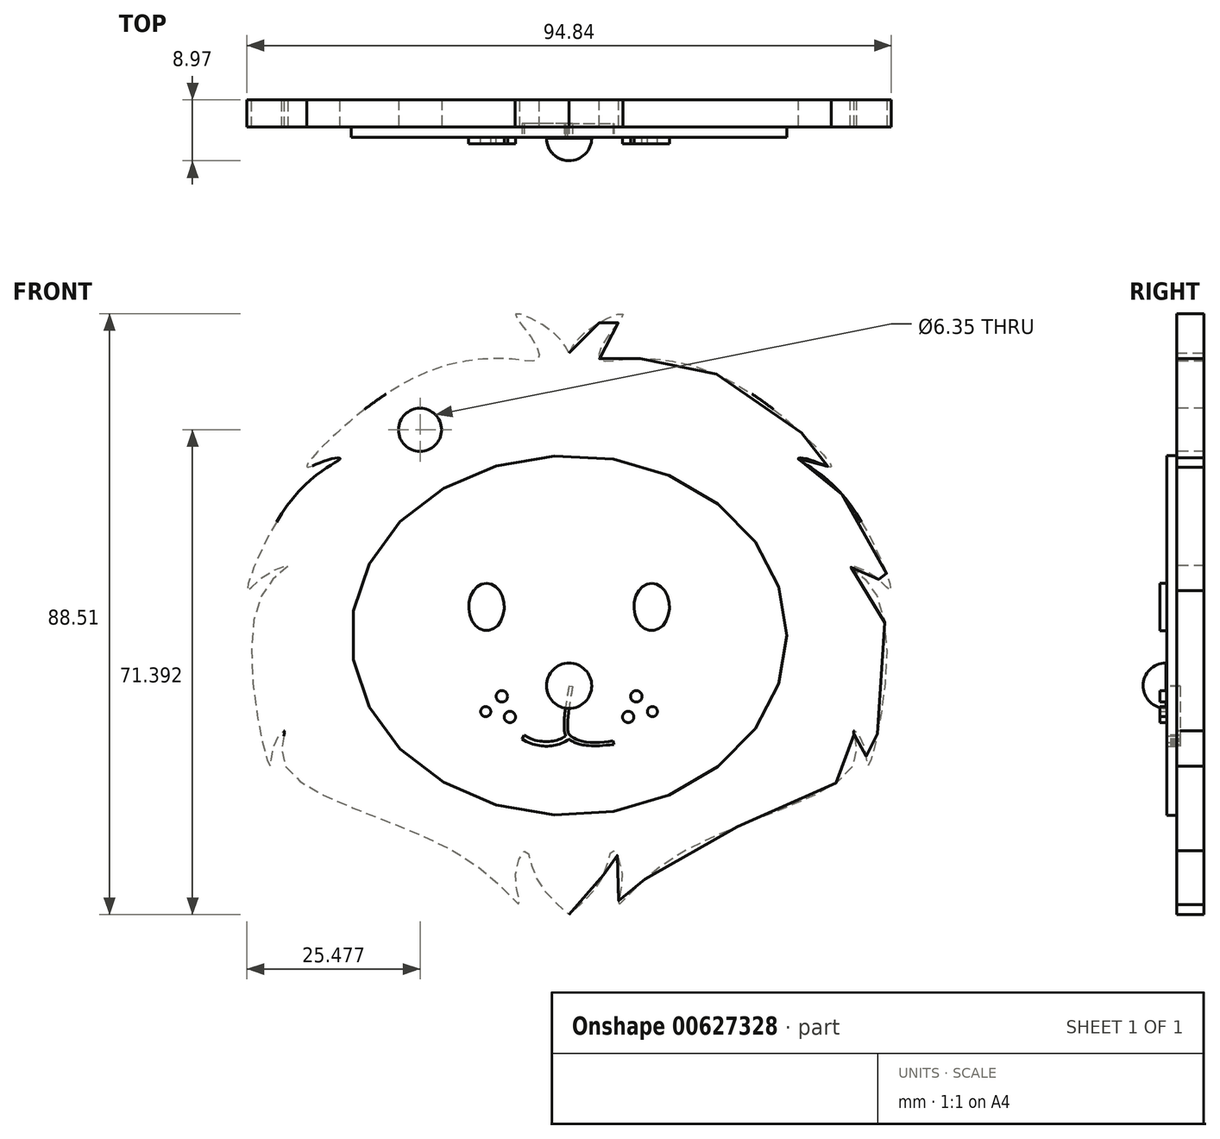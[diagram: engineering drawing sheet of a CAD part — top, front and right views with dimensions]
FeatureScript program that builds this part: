
annotation { "Feature Type Name" : "Feature", "Feature Type Description" : "" }
export const myFeature = defineFeature(function(context is Context, id is Id, definition is map)
    precondition{}
    {
        {
            var Q0;
            Q0=qCreatedBy(makeId("Front.planeOp"),FACE);
            var sketch = newSketch(context, id + "F0", { "sketchPlane" : qUnion([Q0])});
            skFitSpline(sketch, "E0", {"points": [v(0, 48.97) * mm, v(2.72, 52.32) * mm, v(7.89, 54.75) * mm, v(5.45, 51.1) * mm, v(4.54, 48.06) * mm, v(8.19, 48.06) * mm, v(24.6, 44.42) * mm, v(38.58, 32.26) * mm, v(35.85, 33.17) * mm, v(33.72, 33.47) * mm, v(40.1, 28.3) * mm, v(47.4, 14.02) * mm, v(44.97, 16.15) * mm, v(41.32, 17.67) * mm, v(45.88, 11.9) * mm, v(44.05, -11.81) * mm, v(43.45, -8.77) * mm, v(41.93, -6.65) * mm, v(41.93, -11.5) * mm, v(15.48, -25.19) * mm, v(7.28, -32.18) * mm, v(7.89, -27.92) * mm, v(6.37, -24.28) * mm, v(5.15, -27.62) * mm, v(0, -33.7) * mm], "startDerivative": vector(53.9, 99.14) * mm, "endDerivative": vector(-141.36, -126.3) * mm});
            skLineSegment(sketch, "E1", {"start": v(0, 48.97) * mm, "end": v(0, -33.46) * mm});
            skFitSpline(sketch, "E2.MirrorCS", {"points": [v(0, 48.97) * mm, v(-2.72, 52.32) * mm, v(-7.89, 54.75) * mm, v(-5.45, 51.1) * mm, v(-4.54, 48.06) * mm, v(-8.19, 48.06) * mm, v(-24.6, 44.42) * mm, v(-38.58, 32.26) * mm, v(-35.85, 33.17) * mm, v(-33.72, 33.47) * mm, v(-40.1, 28.3) * mm, v(-47.4, 14.02) * mm, v(-44.97, 16.15) * mm, v(-41.32, 17.67) * mm, v(-45.88, 11.9) * mm, v(-44.05, -11.81) * mm, v(-43.45, -8.77) * mm, v(-41.93, -6.65) * mm, v(-41.93, -11.5) * mm, v(-15.48, -25.19) * mm, v(-7.28, -32.18) * mm, v(-7.89, -27.92) * mm, v(-6.37, -24.28) * mm, v(-5.15, -27.62) * mm, v(0, -33.7) * mm], "startDerivative": vector(-53.9, 99.14) * mm, "endDerivative": vector(141.36, -126.3) * mm});
            skFitSpline(sketch, "E3.MirrorCS", {"points": [v(0, 48.97) * mm, v(-2.72, 52.32) * mm, v(-7.89, 54.75) * mm, v(-5.45, 51.1) * mm, v(-4.54, 48.06) * mm, v(-8.19, 48.06) * mm, v(-24.6, 44.42) * mm, v(-38.58, 32.26) * mm, v(-35.85, 33.17) * mm, v(-33.72, 33.47) * mm, v(-40.1, 28.3) * mm, v(-47.4, 14.02) * mm, v(-44.97, 16.15) * mm, v(-41.32, 17.67) * mm, v(-45.88, 11.9) * mm, v(-44.05, -11.81) * mm, v(-43.45, -8.77) * mm, v(-41.93, -6.65) * mm, v(-41.93, -11.5) * mm, v(-15.48, -25.19) * mm, v(-7.28, -32.18) * mm, v(-7.89, -27.92) * mm, v(-6.37, -24.28) * mm, v(-5.15, -27.62) * mm, v(0, -33.7) * mm], "startDerivative": vector(-53.9, 99.14) * mm, "endDerivative": vector(141.36, -126.3) * mm});
            skSolve(sketch);
        }
        {
            var Q0;
            Q0=makeQuery(id+"F0.imprint","IMPRINT",FACE,{"disambiguationData":[TD([[makeQuery(id+"F0.imprint","IMPRINT",EDGE,{"derivedFrom":sQuery(id+"F0.wireOp",EDGE,"E0")}),-1.0]])]});
            var Q1;
            Q1 = qSketchRegion(id + "F0", true);
            extrude(context, id + "F1", {"entities" : qUnion([Q0, Q1]), "depth" : 4 * mm, "offsetDistance" : 25.4 * mm});
        }
        {
            var Q0;
            Q0=makeQuery(id+"F1.opExtrude","CAP_FACE",FACE,{"disambiguationData":[OSD([sQuery(id+"F0.wireOp",EDGE,"E0"),sQuery(id+"F0.wireOp",EDGE,"E3.MirrorCS")])],"isStart":false});
            var sketch = newSketch(context, id + "F2", { "sketchPlane" : qUnion([Q0])});
            skEllipse(sketch, "E4", {"center": v(0, 7.43) * mm, "majorRadius": 32.07 * mm, "minorRadius": 26.48 * mm, "majorAxis": v(1, 0)});
            skSolve(sketch);
        }
        {
            var Q0;
            Q0 = qSketchRegion(id + "F2", true);
            extrude(context, id + "F3", {"entities" : qUnion([Q0]), "operationType" : NewBodyOperationType.ADD, "depth" : 1.5 * mm, "offsetDistance" : 25.4 * mm});
        }
        {
            var Q0;
            Q0=qCreatedBy(makeId("Top.planeOp"),FACE);
            var sketch = newSketch(context, id + "F4", { "sketchPlane" : qUnion([Q0])});
            skArc(sketch, "E5", {"start": v(0, -8.97) * mm, "mid": v(2.36, -8) * mm, "end": v(3.33, -5.63) * mm});
            skLineSegment(sketch, "E6", {"start": v(0, -8.97) * mm, "end": v(0, -5.63) * mm});
            skLineSegment(sketch, "E7", {"start": v(0, -5.63) * mm, "end": v(3.33, -5.63) * mm});
            skSolve(sketch);
        }
        {
            var Q0;
            Q0 = qSketchRegion(id + "F4", true);
            var Q1;
            Q1=sQuery(id+"F4.wireOp",EDGE,"E6");
            revolve(context, id + "F5", {"entities" : qUnion([Q0]), "axis" : qUnion([Q1]), "revolveType" : RevolveType.FULL});
        }
        {
            var Q0;
            Q0=makeQuery(id+"F3.opExtrude","CAP_FACE",FACE,{"disambiguationData":[OSD([sQuery(id+"F2.wireOp",EDGE,"E4")])],"isStart":false});
            var sketch = newSketch(context, id + "F6", { "sketchPlane" : qUnion([Q0])});
            skEllipse(sketch, "E8", {"center": v(-12.16, 11.61) * mm, "majorRadius": 3.5 * mm, "minorRadius": 2.61 * mm, "majorAxis": v(0, 1)});
            skEllipse(sketch, "E9.MirrorC", {"center": v(12.16, 11.61) * mm, "majorRadius": 3.5 * mm, "minorRadius": 2.61 * mm, "majorAxis": v(0, 1)});
            skSolve(sketch);
        }
        {
            var Q0;
            Q0 = qSketchRegion(id + "F6", true);
            extrude(context, id + "F7", {"entities" : qUnion([Q0]), "operationType" : NewBodyOperationType.ADD, "depth" : 1 * mm, "offsetDistance" : 25.4 * mm});
        }
        {
            var Q0;
            Q0=makeQuery(id+"F3.opExtrude","CAP_FACE",FACE,{"disambiguationData":[OSD([sQuery(id+"F2.wireOp",EDGE,"E4")])],"isStart":false});
            var sketch = newSketch(context, id + "F8", { "sketchPlane" : qUnion([Q0])});
            skCircle(sketch, "E10", {"center": v(9.9, -1.56) * mm, "radius": 0.84 * mm});
            skCircle(sketch, "E11", {"center": v(12.27, -3.8) * mm, "radius": 0.75 * mm});
            skCircle(sketch, "E12", {"center": v(8.71, -4.59) * mm, "radius": 0.83 * mm});
            skCircle(sketch, "E13.MirrorC", {"center": v(-9.9, -1.56) * mm, "radius": 0.84 * mm});
            skCircle(sketch, "E14.MirrorC", {"center": v(-12.27, -3.8) * mm, "radius": 0.75 * mm});
            skCircle(sketch, "E15.MirrorC", {"center": v(-8.71, -4.59) * mm, "radius": 0.83 * mm});
            skSolve(sketch);
        }
        {
            var Q0;
            Q0 = qSketchRegion(id + "F8", true);
            extrude(context, id + "F9", {"entities" : qUnion([Q0]), "operationType" : NewBodyOperationType.ADD, "depth" : 1 * mm, "offsetDistance" : 25.4 * mm});
        }
        {
            var Q0;
            Q0=makeQuery(id+"F1.opExtrude","CAP_FACE",FACE,{"disambiguationData":[OSD([sQuery(id+"F0.wireOp",EDGE,"E0"),sQuery(id+"F0.wireOp",EDGE,"E3.MirrorCS")])],"isStart":false});
            var sketch = newSketch(context, id + "F10", { "sketchPlane" : qUnion([Q0])});
            skCircle(sketch, "E16", {"center": v(-21.94, 37.7) * mm, "radius": 3.8 * mm});
            skSolve(sketch);
        }
        {
            var Q0;
            Q0=sQuery(id+"F10.wireOp",VERTEX,"E16.center");
            var Q1;
            Q1=makeQuery(id+"F1.opExtrude","SWEPT_BODY",BODY,{"disambiguationData":[OSD([sQuery(id+"F0.wireOp",EDGE,"E0"),sQuery(id+"F0.wireOp",EDGE,"E3.MirrorCS")])]});
            hole(context, id + "F11", {"style" : HoleStyle.SIMPLE, "endStyle" : HoleEndStyle.THROUGH, "holeDiameter" : 6.35 * mm, "majorDiameter" : 6.35 * mm, "isTappedThrough" : true, "tappedDepth" : 12.7 * mm, "tapClearance" : 3, "locations" : qUnion([Q0]), "scope" : qUnion([Q1])});
        }
        {
            var Q0;
            Q0=makeQuery(id+"F3.opExtrude","CAP_FACE",FACE,{"disambiguationData":[OSD([sQuery(id+"F2.wireOp",EDGE,"E4")])],"isStart":false});
            var sketch = newSketch(context, id + "F12", { "sketchPlane" : qUnion([Q0])});
            skFitSpline(sketch, "E17", {"points": [v(0, 0) * mm, v(-0.64, -6.92) * mm, v(0, -7.85) * mm, v(6.57, -8.63) * mm], "startDerivative": vector(-3.49, -17.73) * mm, "endDerivative": vector(32.8, 4.3) * mm});
            skFitSpline(sketch, "E18", {"points": [v(0, -7.85) * mm, v(-3.2, -8.88) * mm, v(-6.95, -7.85) * mm], "startDerivative": vector(-6.45, -4.56) * mm, "endDerivative": vector(-7.43, 4.46) * mm});
            skFitSpline(sketch, "E19.0", {"points": [v(-0.4, -7.3) * mm, v(-0.64, -7.46) * mm, v(-1.11, -7.74) * mm, v(-1.82, -8.01) * mm, v(-2.55, -8.17) * mm, v(-3.32, -8.21) * mm, v(-4.11, -8.16) * mm, v(-5.2, -7.95) * mm, v(-6.03, -7.6) * mm, v(-6.6, -7.26) * mm]});
            skFitSpline(sketch, "E20.0", {"points": [v(0.52, -0.1) * mm, v(0.38, -0.83) * mm, v(0.17, -2.02) * mm, v(-0.04, -3.58) * mm, v(-0.15, -4.68) * mm, v(-0.2, -5.66) * mm, v(-0.19, -6.32) * mm, v(-0.14, -6.71) * mm, v(-0.1, -6.93) * mm, v(-0.04, -7.06) * mm, v(0.01, -7.15) * mm, v(0.08, -7.23) * mm, v(0.17, -7.3) * mm, v(0.26, -7.38) * mm, v(0.36, -7.46) * mm, v(0.5, -7.56) * mm, v(0.7, -7.68) * mm, v(0.98, -7.83) * mm, v(1.43, -8.02) * mm, v(2.19, -8.2) * mm, v(3.6, -8.35) * mm, v(5.16, -8.28) * mm, v(6.5, -8.1) * mm]});
            skLineSegment(sketch, "E21", {"start": v(6.5, -8.1) * mm, "end": v(6.57, -8.63) * mm});
            skLineSegment(sketch, "E22", {"start": v(0, 0) * mm, "end": v(0.52, -0.1) * mm});
            skLineSegment(sketch, "E23", {"start": v(-6.6, -7.26) * mm, "end": v(-6.95, -7.85) * mm});
            skPoint(sketch, "E24", {"position": v(-0.5, -7.32) * mm});
            skLineSegment(sketch, "E25", {"start": v(-0.59, -7.42) * mm, "end": v(-0.5, -7.32) * mm});
            skSolve(sketch);
        }
        {
            var Q0;
            Q0 = qSketchRegion(id + "F12", true);
            extrude(context, id + "F13", {"entities" : qUnion([Q0]), "operationType" : NewBodyOperationType.REMOVE, "oppositeDirection" : true, "depth" : 1 * mm, "offsetDistance" : 25.4 * mm});
        }
        {
            var Q0;
            Q0=makeQuery(id+"F13.boolean.opBoolean","COPY",FACE,{"derivedFrom":makeQuery(id+"F13.opExtrude","CAP_FACE",FACE,{"disambiguationData":[OSD([sQuery(id+"F12.wireOp",EDGE,"E17"),sQuery(id+"F12.wireOp",EDGE,"E18"),sQuery(id+"F12.wireOp",EDGE,"E19.0"),sQuery(id+"F12.wireOp",EDGE,"E20.0"),sQuery(id+"F12.wireOp",EDGE,"E21"),sQuery(id+"F12.wireOp",EDGE,"E22"),sQuery(id+"F12.wireOp",EDGE,"E23"),sQuery(id+"F12.wireOp",EDGE,"E25"),sQuery(id+"F12.wireOp",EDGE,"E17")])],"isStart":false})});
            extrude(context, id + "F14", {"entities" : qUnion([Q0]), "operationType" : NewBodyOperationType.REMOVE, "oppositeDirection" : true, "depth" : 1 * mm, "offsetDistance" : 25.4 * mm});
        }
    });
